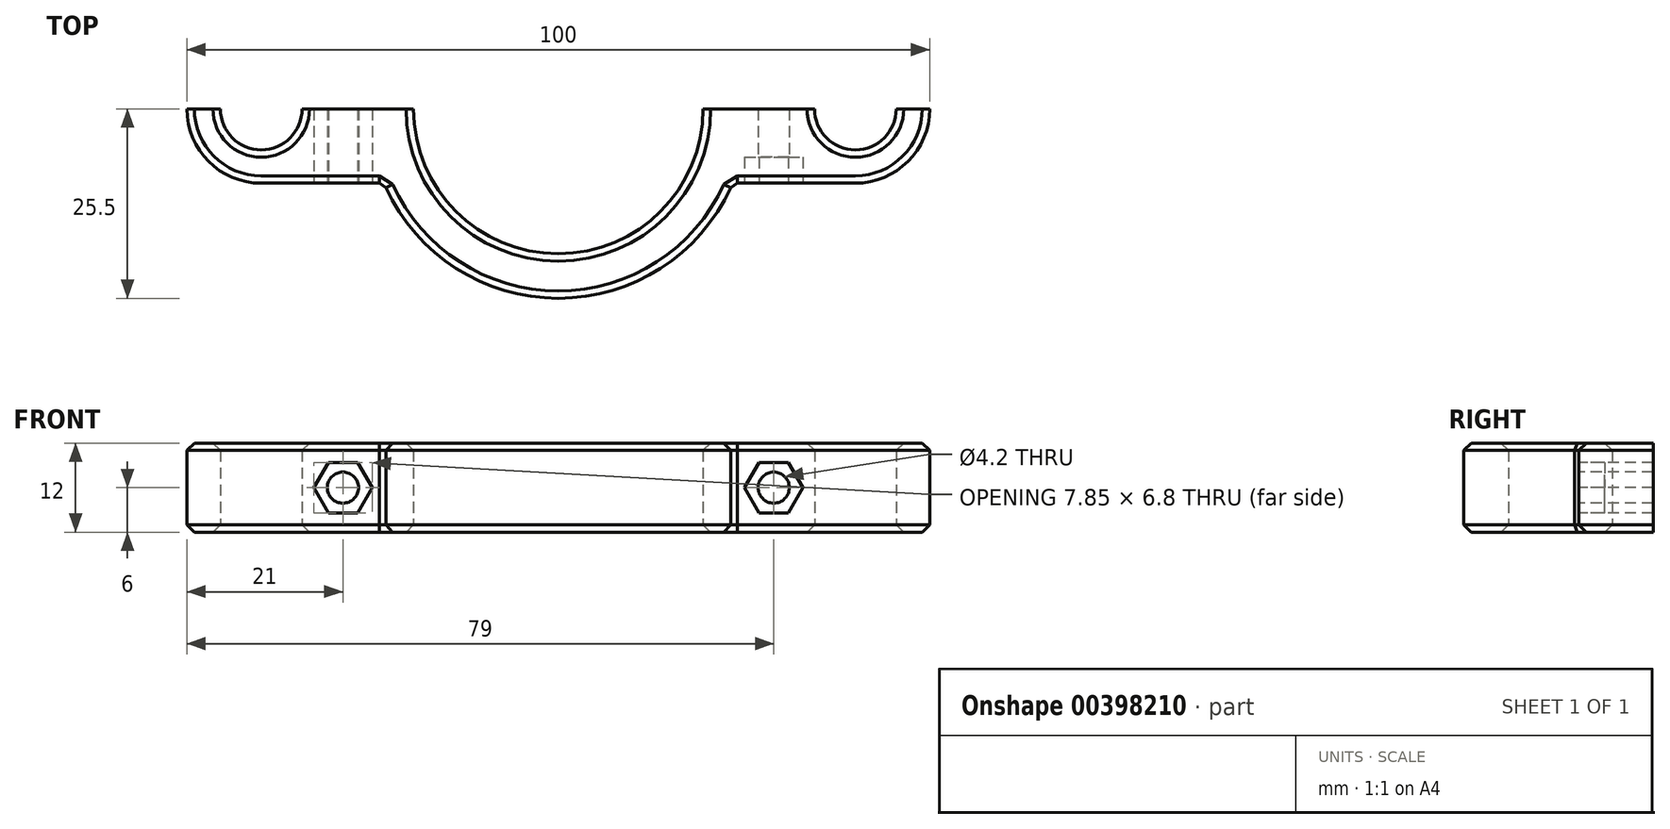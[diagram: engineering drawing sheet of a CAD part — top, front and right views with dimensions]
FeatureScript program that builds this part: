
annotation { "Feature Type Name" : "Feature", "Feature Type Description" : "" }
export const myFeature = defineFeature(function(context is Context, id is Id, definition is map)
    precondition{}
    {
        {
            var Q0;
            Q0=qCreatedBy(makeId("Top.planeOp"),FACE);
            var sketch = newSketch(context, id + "F0", { "sketchPlane" : qUnion([Q0])});
            skArc(sketch, "E0", {"start": v(-19.5, 0) * mm, "mid": v(0, -19.5) * mm, "end": v(19.5, 0) * mm});
            skArc(sketch, "E1", {"start": v(-50, 0) * mm, "mid": v(-47.07, -7.07) * mm, "end": v(-40, -10) * mm});
            skArc(sketch, "E2", {"start": v(-45.5, 0) * mm, "mid": v(-40, -5.5) * mm, "end": v(-34.5, 0) * mm});
            skArc(sketch, "E3.MirrorC", {"start": v(50, 0) * mm, "mid": v(47.07, -7.07) * mm, "end": v(40, -10) * mm});
            skArc(sketch, "E4.MirrorC", {"start": v(45.5, 0) * mm, "mid": v(40, -5.5) * mm, "end": v(34.5, 0) * mm});
            skArc(sketch, "E5", {"start": v(-23.46, -10) * mm, "mid": v(0, -25.5) * mm, "end": v(23.46, -10) * mm});
            skLineSegment(sketch, "E6", {"start": v(-40, -10) * mm, "end": v(-23.46, -10) * mm});
            skLineSegment(sketch, "E7", {"start": v(0, 0) * mm, "end": v(0, 37.42) * mm, "construction": true});
            skLineSegment(sketch, "E8.MirrorCS", {"start": v(40, -10) * mm, "end": v(23.46, -10) * mm});
            skLineSegment(sketch, "E9", {"start": v(-50, 0) * mm, "end": v(-45.5, 0) * mm});
            skLineSegment(sketch, "E10", {"start": v(-34.5, 0) * mm, "end": v(-19.5, 0) * mm});
            skLineSegment(sketch, "E11", {"start": v(19.5, 0) * mm, "end": v(34.5, 0) * mm});
            skLineSegment(sketch, "E12", {"start": v(45.5, 0) * mm, "end": v(50, 0) * mm});
            skSolve(sketch);
        }
        {
            var Q0;
            Q0 = qSketchRegion(id + "F0", true);
            extrude(context, id + "F1", {"entities" : qUnion([Q0]), "endBound" : BoundingType.SYMMETRIC, "depth" : 12 * mm, "offsetDistance" : 25 * mm, "flatOperationType" : FlatOperationType.REMOVE, "domain" : OperationDomain.MODEL});
        }
        {
            var Q0;
            Q0=makeQuery(id+"F1.opExtrude","SWEPT_FACE",FACE,{"disambiguationData":[OSD([sQuery(id+"F0.wireOp",EDGE,"E8.MirrorCS")])]});
            cPlane(context, id + "F2", {"entities" : qUnion([Q0]), "cplaneType" : CPlaneType.OFFSET, "offset" : 0 * mm, "width" : 150 * mm, "height" : 150 * mm});
        }
        {
            var Q0;
            Q0=qCreatedBy(id+"F2.planeOp",FACE);
            var sketch = newSketch(context, id + "F3", { "sketchPlane" : qUnion([Q0])});
            skCircle(sketch, "E13.cCircle", {"center": v(29, 0) * mm, "radius": 3.4 * mm, "construction": true});
            skLineSegment(sketch, "E13.0", {"start": v(30.96, 3.4) * mm, "end": v(32.93, 0) * mm});
            skLineSegment(sketch, "E13.1", {"start": v(32.93, 0) * mm, "end": v(30.96, -3.4) * mm});
            skLineSegment(sketch, "E13.2", {"start": v(30.96, -3.4) * mm, "end": v(27.04, -3.4) * mm});
            skLineSegment(sketch, "E13.3", {"start": v(27.04, -3.4) * mm, "end": v(25.07, 0) * mm});
            skLineSegment(sketch, "E13.4", {"start": v(25.07, 0) * mm, "end": v(27.04, 3.4) * mm});
            skLineSegment(sketch, "E13.5", {"start": v(27.04, 3.4) * mm, "end": v(30.96, 3.4) * mm});
            skPoint(sketch, "E13.0.midPoint", {"position": v(31.94, 1.7) * mm});
            skCircle(sketch, "E14", {"center": v(29, 0) * mm, "radius": 2.1 * mm});
            skLineSegment(sketch, "E15", {"start": v(0, 0) * mm, "end": v(0, 29.28) * mm, "construction": true});
            skLineSegment(sketch, "E16", {"start": v(0, 0) * mm, "end": v(0, -20.32) * mm, "construction": true});
            skLineSegment(sketch, "E17.MirrorCS", {"start": v(-27.04, 3.4) * mm, "end": v(-30.96, 3.4) * mm});
            skLineSegment(sketch, "E18.MirrorCS", {"start": v(-25.07, 0) * mm, "end": v(-27.04, 3.4) * mm});
            skLineSegment(sketch, "E19.MirrorCS", {"start": v(-27.04, -3.4) * mm, "end": v(-25.07, 0) * mm});
            skCircle(sketch, "E20.MirrorC", {"center": v(-29, 0) * mm, "radius": 2.1 * mm});
            skLineSegment(sketch, "E21.MirrorCS", {"start": v(-30.96, -3.4) * mm, "end": v(-27.04, -3.4) * mm});
            skLineSegment(sketch, "E22.MirrorCS", {"start": v(-32.93, 0) * mm, "end": v(-30.96, -3.4) * mm});
            skLineSegment(sketch, "E23.MirrorCS", {"start": v(-30.96, 3.4) * mm, "end": v(-32.93, 0) * mm});
            skCircle(sketch, "E24.MirrorC", {"center": v(-29, 0) * mm, "radius": 3.4 * mm, "construction": true});
            skSolve(sketch);
        }
        {
            var Q0;
            Q0=makeQuery(id+"F1.opExtrude","SWEPT_FACE",FACE,{"disambiguationData":[OSD([sQuery(id+"F0.wireOp",EDGE,"E5")])]});
            var Q1;
            Q1=makeQuery(id+"F1.opExtrude","CAP_EDGE",EDGE,{"disambiguationData":[OSD([sQuery(id+"F0.wireOp",EDGE,"E2")])],"isStart":false});
            var Q2;
            Q2=makeQuery(id+"F1.opExtrude","CAP_EDGE",EDGE,{"disambiguationData":[OSD([sQuery(id+"F0.wireOp",EDGE,"E2")])],"isStart":true});
            var Q3;
            Q3=makeQuery(id+"F1.opExtrude","CAP_EDGE",EDGE,{"disambiguationData":[OSD([sQuery(id+"F0.wireOp",EDGE,"E4.MirrorC")])],"isStart":false});
            var Q4;
            Q4=makeQuery(id+"F1.opExtrude","CAP_EDGE",EDGE,{"disambiguationData":[OSD([sQuery(id+"F0.wireOp",EDGE,"E4.MirrorC")])],"isStart":true});
            var Q5;
            Q5=makeQuery(id+"F1.opExtrude","CAP_EDGE",EDGE,{"disambiguationData":[OSD([sQuery(id+"F0.wireOp",EDGE,"E0")])],"isStart":true});
            var Q6;
            Q6=makeQuery(id+"F1.opExtrude","CAP_EDGE",EDGE,{"disambiguationData":[OSD([sQuery(id+"F0.wireOp",EDGE,"E0")])],"isStart":false});
            chamfer(context, id + "F4", {"entities" : qUnion([Q0, Q1, Q2, Q3, Q4, Q5, Q6]), "width" : 1 * mm, "tangentPropagation" : true});
        }
        {
            var Q0;
            Q0 = qSketchRegion(id + "F3", true);
            extrude(context, id + "F5", {"entities" : qUnion([Q0]), "operationType" : NewBodyOperationType.REMOVE, "flatOperationType" : FlatOperationType.REMOVE, "oppositeDirection" : true, "depth" : 3.5 * mm, "offsetDistance" : 25 * mm, "domain" : OperationDomain.MODEL});
        }
        {
            var Q0;
            Q0=makeQuery(id+"F3.imprint","IMPRINT",FACE,{"disambiguationData":[TD([[makeQuery(id+"F3.imprint","IMPRINT",EDGE,{"derivedFrom":sQuery(id+"F3.wireOp",EDGE,"E14")}),1.0]])]});
            var Q1;
            Q1=makeQuery(id+"F3.imprint","IMPRINT",FACE,{"disambiguationData":[TD([[makeQuery(id+"F3.imprint","IMPRINT",EDGE,{"derivedFrom":sQuery(id+"F3.wireOp",EDGE,"E20.MirrorC")}),-1.0]])]});
            extrude(context, id + "F6", {"entities" : qUnion([Q0, Q1]), "operationType" : NewBodyOperationType.REMOVE, "flatOperationType" : FlatOperationType.REMOVE, "oppositeDirection" : true, "depth" : 25 * mm, "offsetDistance" : 25 * mm, "domain" : OperationDomain.MODEL});
        }
    });
